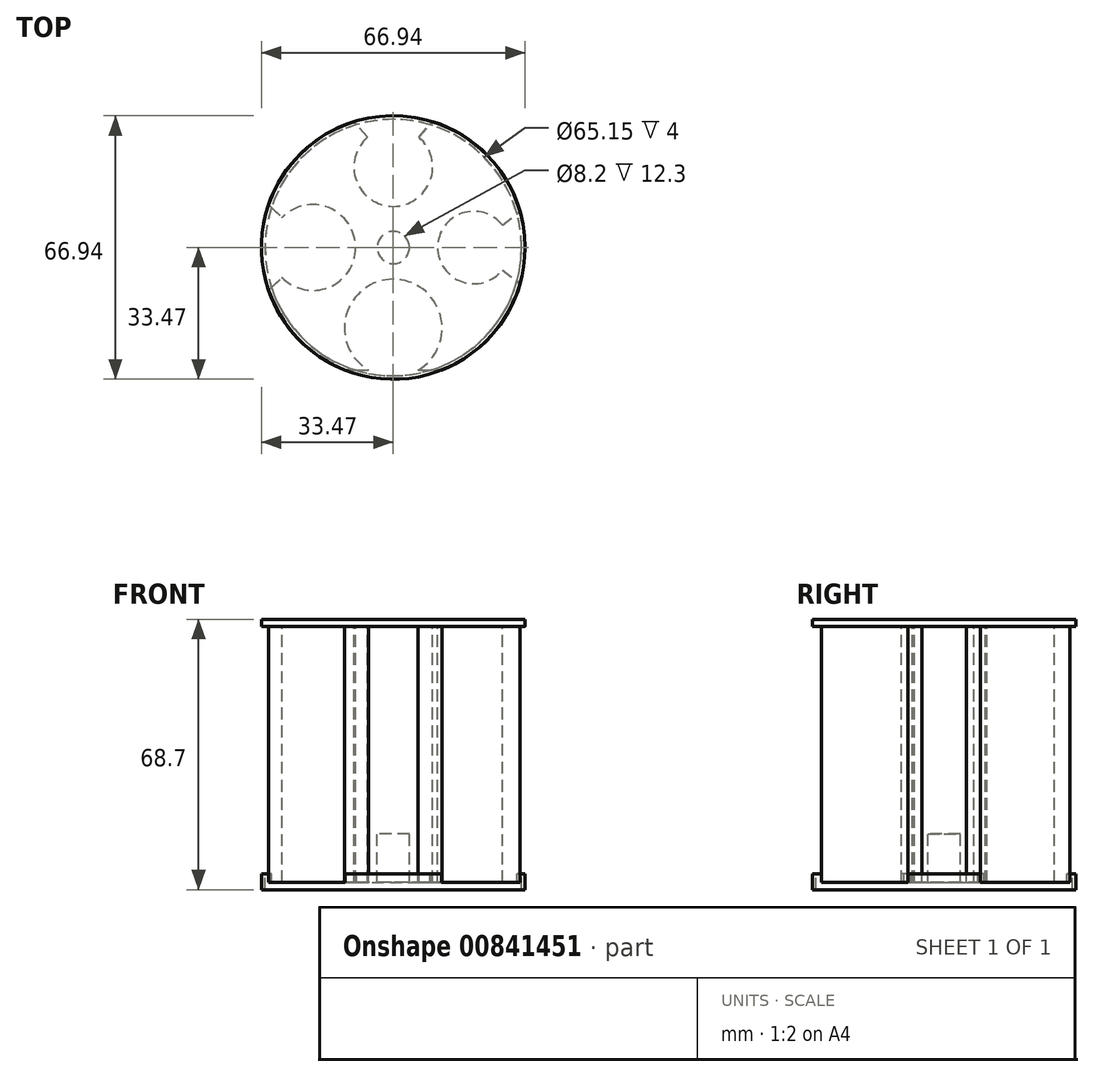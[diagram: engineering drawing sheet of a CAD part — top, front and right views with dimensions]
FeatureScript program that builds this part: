
annotation { "Feature Type Name" : "Feature", "Feature Type Description" : "" }
export const myFeature = defineFeature(function(context is Context, id is Id, definition is map)
    precondition{}
    {
        {
            var Q0;
            Q0=qCreatedBy(makeId("Top.planeOp"),FACE);
            var sketch = newSketch(context, id + "F0", { "sketchPlane" : qUnion([Q0])});
            skArc(sketch, "E0", {"start": v(6.3, -31.13) * mm, "mid": v(0, -8.06) * mm, "end": v(-6.3, -31.13) * mm});
            skArc(sketch, "E1", {"start": v(-6.55, 28.01) * mm, "mid": v(0, 10.46) * mm, "end": v(6.55, 28.01) * mm});
            skArc(sketch, "E2", {"start": v(-28.28, -7.59) * mm, "mid": v(-9.56, 0) * mm, "end": v(-28.28, 7.59) * mm});
            skArc(sketch, "E3", {"start": v(27.7, 5.67) * mm, "mid": v(11.26, 0) * mm, "end": v(27.7, -5.67) * mm});
            skArc(sketch, "E4", {"start": v(-10, 31.99) * mm, "mid": v(-23.36, 24.03) * mm, "end": v(-31.7, 10.9) * mm});
            skLineSegment(sketch, "E5", {"start": v(6.55, 28.01) * mm, "end": v(10, 31.99) * mm});
            skLineSegment(sketch, "E6", {"start": v(-6.55, 28.01) * mm, "end": v(-10, 31.99) * mm});
            skLineSegment(sketch, "E7", {"start": v(27.7, -5.67) * mm, "end": v(32.23, -9.2) * mm});
            skLineSegment(sketch, "E8", {"start": v(27.7, 5.67) * mm, "end": v(32.23, 9.2) * mm});
            skArc(sketch, "E9.trimOffspring", {"start": v(32.23, 9.2) * mm, "mid": v(24, 23.4) * mm, "end": v(10, 31.99) * mm});
            skPoint(sketch, "E10.start.orphan", {"position": v(20.46, -9.2) * mm});
            skLineSegment(sketch, "E11", {"start": v(-12.4, -31.13) * mm, "end": v(-6.3, -31.13) * mm});
            skArc(sketch, "E12.trimOffspring", {"start": v(12.4, -31.13) * mm, "mid": v(24.86, -22.47) * mm, "end": v(32.23, -9.2) * mm});
            skLineSegment(sketch, "E13.trimOffspring", {"start": v(6.3, -31.13) * mm, "end": v(12.4, -31.13) * mm});
            skLineSegment(sketch, "E14", {"start": v(-31.7, -10.9) * mm, "end": v(-28.28, -7.59) * mm});
            skLineSegment(sketch, "E15", {"start": v(-31.7, 10.9) * mm, "end": v(-28.28, 7.59) * mm});
            skArc(sketch, "E16.trimOffspring", {"start": v(-31.7, -10.9) * mm, "mid": v(-24.26, -23.13) * mm, "end": v(-12.4, -31.13) * mm});
            skSolve(sketch);
        }
        {
            var Q0;
            Q0 = qSketchRegion(id + "F0", true);
            extrude(context, id + "F1", {"entities" : qUnion([Q0]), "oppositeDirection" : true, "depth" : 65 * mm, "offsetDistance" : 25 * mm});
        }
        {
            var Q0;
            Q0=qCreatedBy(makeId("Top.planeOp"),FACE);
            var sketch = newSketch(context, id + "F2", { "sketchPlane" : qUnion([Q0])});
            skCircle(sketch, "E17", {"center": v(0, 0) * mm, "radius": 33.47 * mm});
            skSolve(sketch);
        }
        {
            var Q0;
            Q0 = qSketchRegion(id + "F2", true);
            extrude(context, id + "F3", {"entities" : qUnion([Q0]), "operationType" : NewBodyOperationType.ADD, "depth" : 1.8 * mm, "offsetDistance" : 25 * mm});
        }
        {
            var Q0;
            Q0=qCreatedBy(makeId("Top.planeOp"),FACE);
            var sketch = newSketch(context, id + "F4", { "sketchPlane" : qUnion([Q0])});
            skCircle(sketch, "E18", {"center": v(0, 0) * mm, "radius": 33.47 * mm});
            skCircle(sketch, "E19", {"center": v(0, 0) * mm, "radius": 32.57 * mm});
            skSolve(sketch);
        }
        {
            var Q0;
            Q0 = qSketchRegion(id + "F4", true);
            extrude(context, id + "F5", {"entities" : qUnion([Q0]), "operationType" : NewBodyOperationType.ADD, "oppositeDirection" : true, "depth" : 66.9 * mm, "offsetDistance" : 25 * mm, "hasSecondDirection" : true, "secondDirectionOppositeDirection" : true, "secondDirectionDepth" : 62.9 * mm});
        }
        {
            var Q0;
            Q0=qCreatedBy(makeId("Top.planeOp"),FACE);
            var sketch = newSketch(context, id + "F6", { "sketchPlane" : qUnion([Q0])});
            skCircle(sketch, "E20", {"center": v(0, 0) * mm, "radius": 4.1 * mm});
            skSolve(sketch);
        }
        {
            var Q0;
            Q0 = qSketchRegion(id + "F6", true);
            extrude(context, id + "F7", {"entities" : qUnion([Q0]), "operationType" : NewBodyOperationType.REMOVE, "oppositeDirection" : true, "depth" : 65 * mm, "offsetDistance" : 25 * mm, "hasSecondDirection" : true, "secondDirectionOppositeDirection" : true, "secondDirectionDepth" : 52.7 * mm});
        }
    });
